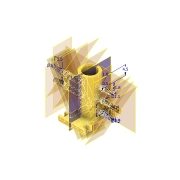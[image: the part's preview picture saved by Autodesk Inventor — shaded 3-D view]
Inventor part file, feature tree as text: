
AUTODESK INVENTOR PART (.ipt)
format: ipt  version: 2021 (Build 250183000, 183)  size: 444,928 bytes
history: native  units: in
note: dims shown in document units (in); Inventor stores cm internally (conversion verified against a paired STEP export)
features: plane x16, extrude x10, sketch x10, revolve x5, mirror x4, projected_geometry x3, fillet x2
ambient origin geometry x8: Origin, YZ Plane, XZ Plane, XY Plane, X Axis, Y Axis, Z Axis, Center Point
bodies: Solid1 (feature_tree), Solid2 (feature_tree), Solid4 (feature_tree), Solid6 (feature_tree), Solid11 (feature_tree), Solid12 (feature_tree)
feature tree (50):
  extrude  "Extrusion1"  Depth=0.315in
  plane  "Work Plane1"
  sketch  "Sketch2"  dims[d2=0.748in d3=0.0in d4=0.2362in]
  extrude  "Extrusion2"  Depth=0.748in
  extrude  "Extrusion3"  Depth=0.0709in
  sketch  "Sketch3"  dims[d5=0.0709in d7=0.0709in]
  revolve  "Revolution1"  [1 undecoded]
  revolve  "Revolution3"  [1 undecoded]
  plane  "Work Plane2"
  plane  "Work Plane7"
  extrude  "Extrusion4"  Depth=0.0433in
  sketch  "Sketch6"  dims[d16=0.0197in d18=0.0197in]
  revolve  "Revolution5"  [1 undecoded]
  plane  "Work Plane8"
  plane  "Work Plane9"
  plane  "Work Plane10"
  plane  "Work Plane14"
  plane  "Work Plane15"
  plane  "Work Plane16"
  mirror  "Mirror1"
  mirror  "Mirror2"
  revolve  "Revolution9"  [1 undecoded]
  plane  "Work Plane17"
  revolve  "Revolution10"  Angle=90.0deg
  plane  "Work Plane19"
  plane  "Work Plane20"
  extrude  "Extrusion13"  TaperAngle=30.0deg  [1 undecoded]
  extrude  "Extrusion14"  [1 undecoded]
  extrude  "Extrusion18"  Depth=0.0197in
  extrude  "Extrusion19"  Depth=0.0197in
  mirror  "Mirror4"
  mirror  "Mirror5"
  plane  "Work Plane21"
  fillet  "Fillet5"  Radius=0.0709in
  extrude  "Extrusion23"  Depth=0.3937in TaperAngle=0.0deg
  extrude  "Extrusion22"  Depth=0.0197in
  fillet  "Fillet6"  Radius=0.0551in
  sketch  "Sketch1"  dims[d0=0.2354in d1=0.315in]
  sketch  "Sketch4"  dims[d9=0.1772in d14=0.8268in d15=0.0in]
  plane  "Work Plane11"
  plane  "Work Plane12"
  plane  "Work Plane13"
  sketch  "Sketch16"  dims[d20=0.8268in d21=0.0in d23=0.0433in]
  sketch  "Sketch20"  dims[d30=0.0433in d34=0.0551in]
  sketch  "Sketch21"  dims[d35=0.0433in d38=0.0551in]
  sketch  "Sketch24"  dims[d41=0.0394in d42=90.0deg]
  sketch  "Sketch25"  dims[d44=90.0deg d46=30.0deg d51=-0.5118in d52=0.2756in d53=0.0709in d54=0.0709in d56=0.3937in d57=0.0in d62=0.0433in d63=0.0551in d64=0.0433in d71=90.0deg d73=-0.2061in d74=-0.4173in d75=-0.5945in d81=0.1969in d82=0.1969in d103=-0.1181in d104=0.1575in d105=0.0787in d106=0.7874in d108=0.1969in d109=0.3937in d111=0.3937in d113=90.0deg d114=-0.1969in d144=0.0197in d145=0.0709in d146=0.0394in d147=0.0551in d148=0.0866in d149=90.0deg d150=0.2362in d151=0.1378in d152=0.1969in d153=-0.1969in d154=0.3937in d155=0.0in d156=0.0394in d157=0.0984in d158=0.0in d174=0.315in d175=0.7087in d176=0.0787in d177=0.0in d178=0.0394in d179=0.0787in d181=0.0394in d182=0.0787in d183=0.0in d186=0.1378in d187=0.4331in d191=0.0197in d192=0.3937in d193=0.0in d194=0.0512in d195=0.3937in d196=0.0in d197=0.0197in d60=0.0197in d61=0.0344in d184=0.0197in d185=0.0344in]
  projected_geometry  "Project Cut Edges5"
  projected_geometry  "Project Cut Edges9"
  projected_geometry  "Project Cut Edges10"
note: 6 required parameter values undecoded (feature->parameter linkage not recoverable at this tier; creation-order binding heuristic only, values carry confidence <= 0.55)